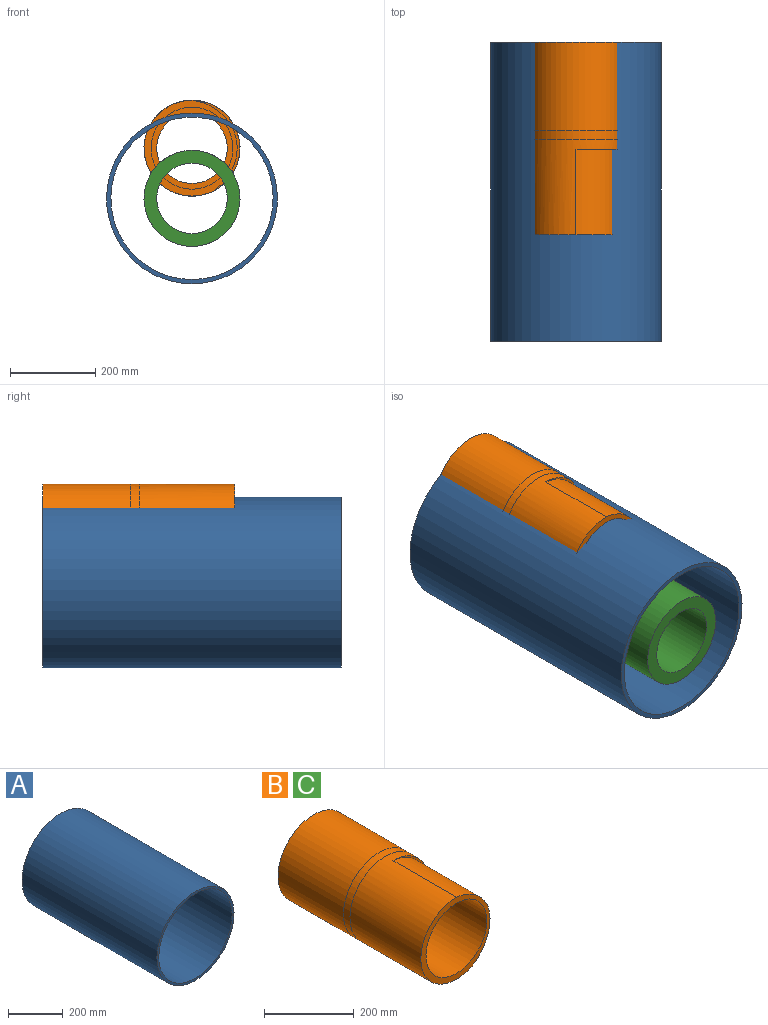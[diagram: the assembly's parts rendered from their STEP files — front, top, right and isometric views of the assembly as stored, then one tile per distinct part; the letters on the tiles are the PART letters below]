
ASSEMBLY  parts=3 mates=3
PART A: 4 faces, bbox 400x700x400 mm
  f0: cylinder r=190mm len=700mm, axis (0,1,0), area 835663.6mm2, adj f2,f3
  f1: cylinder r=200mm len=700mm, axis (0,1,0), area 879645.9mm2, adj f2,f3
  f2: plane 400x400mm, normal (0,-1,0), area 12252.2mm2, adj f0,f1
  f3: plane 400x400mm, normal (0,1,0), area 12252.2mm2, adj f0,f1
PART B: 12 faces, bbox 225x450x225 mm
  f0: plane 191.97x191.97mm, normal (0,-1,0), area 7560.8mm2, adj f1,f9
  f1: cylinder r=82.5mm len=250mm, axis (0,-1,0), area 129590.7mm2, adj f0,f2
  f2: plane 225x225mm, normal (0,1,0), area 18378.3mm2, adj f1,f3
  f3: cylinder r=112.5mm len=225mm, axis (0,-1,0), area 145976mm2, adj f2,f4
  f4: cone r=112.5mm half-angle=1.1deg, axis (0,1,0), area 14115.1mm2, adj f3,f5
  f5: cylinder r=112.11mm len=224.21mm, axis (0,-1,0), area 97173.6mm2, adj f4,f6,f8,f10,f11
  f6: plane 212.83x112.11mm, normal (0,-1,0), area 1373.3mm2, adj f5,f7,f8,f10
  f7: cylinder r=105.86mm len=200mm, axis (0,1,0), area 9442.5mm2, adj f6,f8,f10,f11
  f8: cylinder r=120.73mm len=200mm, axis (0,1,0), area 24065.3mm2, adj f5,f6,f7,f11
  f9: cylinder r=95.98mm len=200mm, axis (0,1,0), area 120617mm2, adj f0,f11
  f10: cylinder r=120.19mm len=200mm, axis (0,1,0), area 24320.4mm2, adj f5,f6,f7,f11
  f11: plane 224.21x217.96mm, normal (0,-1,0), area 9165.9mm2, adj f5,f7,f8,f9,f10
PART C: same geometry as B
PLACE A rot(axis=(1,-0.03,0.03),0deg) t=(75.31,-658.03,8.23)mm fixed
PLACE B rot(axis=(1,-0.03,0.03),0deg) t=(75.31,-884.55,25.71)mm fixed
PLACE C rot(axis=(-1,0,0),180deg) t=(75.31,-1131.52,108.25)mm
MATE revolute C.f1 <-> A.f1  axis (0,1,0) through (75.31,-1108.03,8.23)mm
MATE revolute B.f1 <-> A.f1  axis (0,-1,0) through (75.31,-783.03,125.73)mm
MATE parallel B.f1 <-> A.f0  axis (0,-1,0) through (75.31,-908.03,125.73)mm
